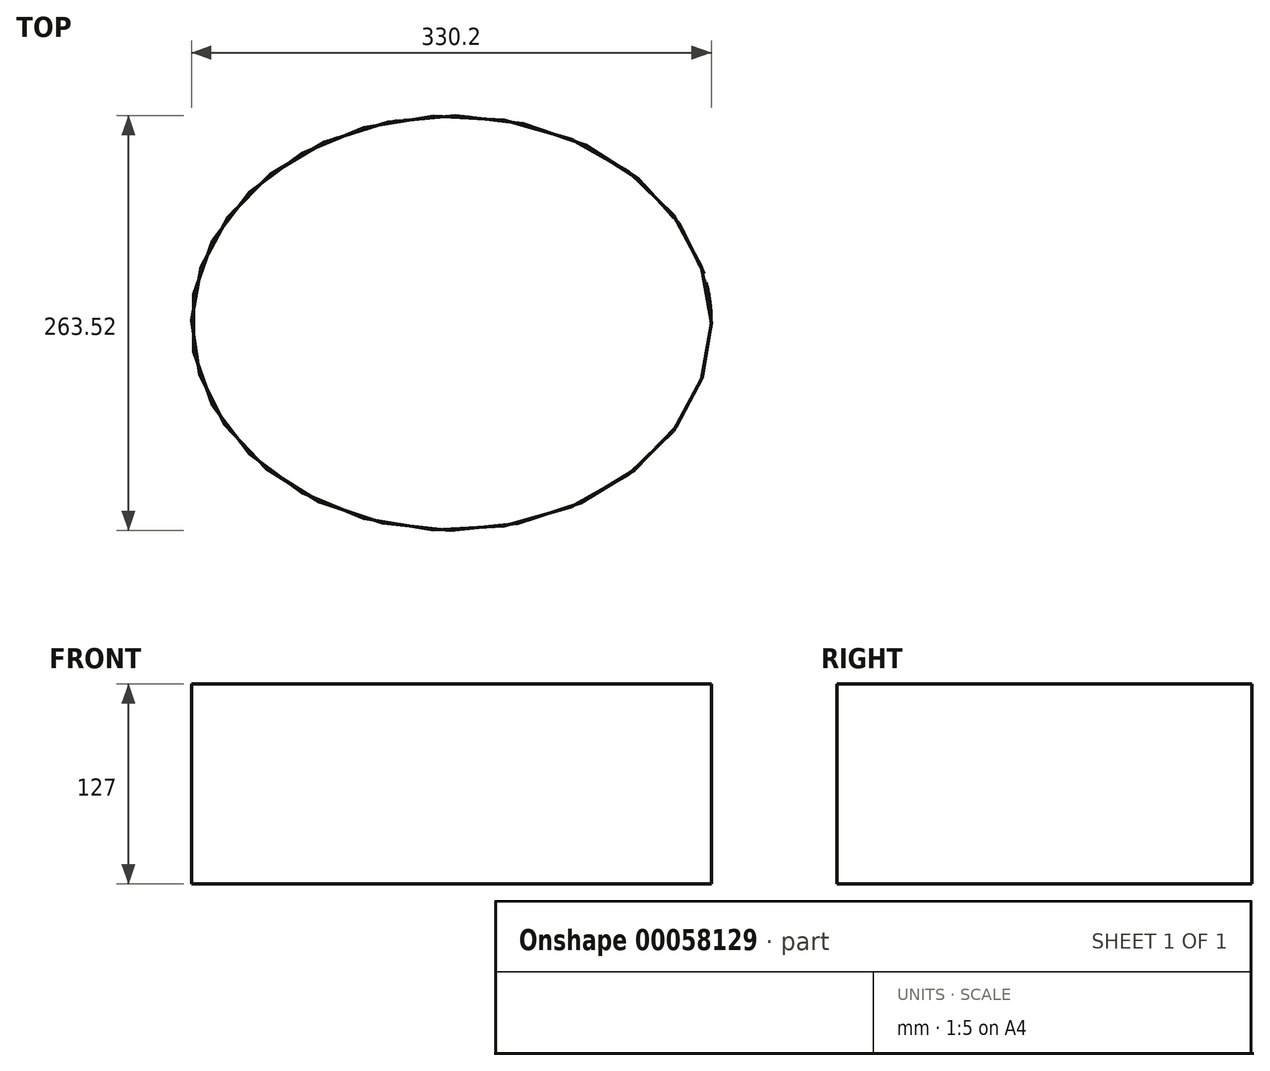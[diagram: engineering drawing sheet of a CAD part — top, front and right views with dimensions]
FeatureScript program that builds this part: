
annotation { "Feature Type Name" : "Feature", "Feature Type Description" : "" }
export const myFeature = defineFeature(function(context is Context, id is Id, definition is map)
    precondition{}
    {
        {
            var Q0;
            Q0=qCreatedBy(makeId("Top.planeOp"),FACE);
            var sketch = newSketch(context, id + "F0", { "sketchPlane" : qUnion([Q0])});
            skEllipse(sketch, "E0", {"center": v(0, 0) * mm, "majorRadius": 165.1 * mm, "minorRadius": 131.76 * mm, "majorAxis": v(1, 0)});
            skFitSpline(sketch, "E1.0", {"points": [v(158.72, -3.08) * mm, v(158.77, 0) * mm, v(158.72, 3.08) * mm, v(158.53, 7.16) * mm, v(158.05, 12.25) * mm, v(157.11, 18.3) * mm, v(155.36, 26.3) * mm, v(152.27, 36.12) * mm, v(147.13, 47.57) * mm, v(140.6, 58.6) * mm, v(134.02, 67.37) * mm, v(128.1, 74.1) * mm, v(123.33, 78.99) * mm, v(119.1, 82.92) * mm, v(115.54, 85.97) * mm, v(112.8, 88.22) * mm, v(109.98, 90.4) * mm, v(106.14, 93.25) * mm, v(101.2, 96.65) * mm, v(95.03, 100.48) * mm, v(86.52, 105.26) * mm, v(75.37, 110.58) * mm, v(61.29, 115.89) * mm, v(46.6, 120.09) * mm, v(33.95, 122.63) * mm, v(23.64, 124.06) * mm, v(15.83, 124.84) * mm, v(9.26, 125.23) * mm, v(3.98, 125.39) * mm, v(0, 125.43) * mm, v(-3.98, 125.39) * mm, v(-9.26, 125.23) * mm, v(-15.83, 124.84) * mm, v(-23.64, 124.06) * mm, v(-33.95, 122.63) * mm, v(-46.6, 120.09) * mm, v(-61.29, 115.89) * mm, v(-75.37, 110.58) * mm, v(-86.52, 105.26) * mm, v(-95.03, 100.48) * mm, v(-101.2, 96.65) * mm, v(-106.14, 93.25) * mm, v(-109.98, 90.4) * mm, v(-112.8, 88.22) * mm, v(-115.54, 85.97) * mm, v(-119.1, 82.92) * mm, v(-123.33, 78.99) * mm, v(-128.1, 74.1) * mm, v(-134.02, 67.37) * mm, v(-140.6, 58.6) * mm, v(-147.13, 47.57) * mm, v(-152.27, 36.12) * mm, v(-155.36, 26.3) * mm, v(-157.11, 18.3) * mm, v(-158.05, 12.25) * mm, v(-158.53, 7.16) * mm, v(-158.72, 3.08) * mm, v(-158.77, 0) * mm, v(-158.72, -3.08) * mm, v(-158.53, -7.16) * mm, v(-158.05, -12.25) * mm, v(-157.11, -18.3) * mm, v(-155.36, -26.3) * mm, v(-152.27, -36.12) * mm, v(-147.13, -47.57) * mm, v(-140.6, -58.6) * mm, v(-134.02, -67.37) * mm, v(-128.1, -74.1) * mm, v(-123.33, -78.99) * mm, v(-119.1, -82.92) * mm, v(-115.54, -85.97) * mm, v(-112.8, -88.22) * mm, v(-109.98, -90.4) * mm, v(-106.14, -93.25) * mm, v(-101.2, -96.65) * mm, v(-95.03, -100.48) * mm, v(-86.52, -105.26) * mm, v(-75.37, -110.58) * mm, v(-61.29, -115.89) * mm, v(-46.6, -120.09) * mm, v(-33.95, -122.63) * mm, v(-23.64, -124.06) * mm, v(-15.83, -124.84) * mm, v(-9.26, -125.23) * mm, v(-3.98, -125.39) * mm, v(0, -125.43) * mm, v(3.98, -125.39) * mm, v(9.26, -125.23) * mm, v(15.83, -124.84) * mm, v(23.64, -124.06) * mm, v(33.95, -122.63) * mm, v(46.6, -120.09) * mm, v(61.29, -115.89) * mm, v(75.37, -110.58) * mm, v(86.52, -105.26) * mm, v(95.03, -100.48) * mm, v(101.2, -96.65) * mm, v(106.14, -93.25) * mm, v(109.98, -90.4) * mm, v(112.8, -88.22) * mm, v(115.54, -85.97) * mm, v(119.1, -82.92) * mm, v(123.33, -78.99) * mm, v(128.1, -74.1) * mm, v(134.02, -67.37) * mm, v(140.6, -58.6) * mm, v(147.13, -47.57) * mm, v(152.27, -36.12) * mm, v(155.36, -26.3) * mm, v(157.11, -18.3) * mm, v(158.05, -12.25) * mm, v(158.53, -7.16) * mm, v(158.72, -3.08) * mm, v(158.77, 0) * mm, v(158.72, 3.08) * mm, v(158.72, -3.08) * mm]});
            skSolve(sketch);
        }
        {
            var Q0;
            Q0=makeQuery(id+"F0.imprint","IMPRINT",FACE,{"disambiguationData":[TD([[makeQuery(id+"F0.imprint","IMPRINT",EDGE,{"derivedFrom":sQuery(id+"F0.wireOp",EDGE,"E0")}),1.0]])]});
            extrude(context, id + "F1", {"entities" : qUnion([Q0]), "depth" : 25.4 * mm});
        }
        {
            var Q0;
            Q0=qCreatedBy(makeId("Top.planeOp"),FACE);
            var sketch = newSketch(context, id + "F2", { "sketchPlane" : qUnion([Q0])});
            skEllipse(sketch, "E2", {"center": v(0, 0) * mm, "majorRadius": 165.1 * mm, "minorRadius": 131.76 * mm, "majorAxis": v(1, 0)});
            skFitSpline(sketch, "E3.0", {"points": [v(158.72, -3.08) * mm, v(158.77, 0) * mm, v(158.72, 3.08) * mm, v(158.53, 7.16) * mm, v(158.05, 12.25) * mm, v(157.1, 18.3) * mm, v(155.36, 26.3) * mm, v(152.27, 36.12) * mm, v(147.13, 47.57) * mm, v(140.6, 58.6) * mm, v(134.02, 67.37) * mm, v(128.1, 74.1) * mm, v(123.33, 78.98) * mm, v(119.1, 82.92) * mm, v(115.54, 85.97) * mm, v(112.8, 88.22) * mm, v(109.98, 90.4) * mm, v(106.14, 93.25) * mm, v(101.2, 96.65) * mm, v(95.03, 100.48) * mm, v(86.52, 105.26) * mm, v(75.37, 110.58) * mm, v(61.29, 115.89) * mm, v(46.6, 120.09) * mm, v(33.95, 122.63) * mm, v(23.64, 124.06) * mm, v(15.83, 124.84) * mm, v(9.26, 125.23) * mm, v(3.98, 125.39) * mm, v(0, 125.43) * mm, v(-3.98, 125.39) * mm, v(-9.26, 125.23) * mm, v(-15.83, 124.84) * mm, v(-23.64, 124.06) * mm, v(-33.95, 122.63) * mm, v(-46.6, 120.09) * mm, v(-61.29, 115.89) * mm, v(-75.37, 110.58) * mm, v(-86.52, 105.26) * mm, v(-95.03, 100.48) * mm, v(-101.2, 96.65) * mm, v(-106.14, 93.25) * mm, v(-109.98, 90.4) * mm, v(-112.8, 88.22) * mm, v(-115.54, 85.97) * mm, v(-119.1, 82.92) * mm, v(-123.33, 78.98) * mm, v(-128.1, 74.1) * mm, v(-134.02, 67.37) * mm, v(-140.6, 58.6) * mm, v(-147.13, 47.57) * mm, v(-152.27, 36.12) * mm, v(-155.36, 26.3) * mm, v(-157.11, 18.3) * mm, v(-158.05, 12.25) * mm, v(-158.53, 7.16) * mm, v(-158.72, 3.08) * mm, v(-158.77, 0) * mm, v(-158.72, -3.08) * mm, v(-158.53, -7.16) * mm, v(-158.05, -12.25) * mm, v(-157.11, -18.3) * mm, v(-155.36, -26.3) * mm, v(-152.27, -36.12) * mm, v(-147.13, -47.57) * mm, v(-140.6, -58.6) * mm, v(-134.02, -67.37) * mm, v(-128.1, -74.1) * mm, v(-123.33, -78.99) * mm, v(-119.1, -82.92) * mm, v(-115.54, -85.97) * mm, v(-112.8, -88.22) * mm, v(-109.98, -90.4) * mm, v(-106.14, -93.25) * mm, v(-101.2, -96.65) * mm, v(-95.03, -100.48) * mm, v(-86.52, -105.26) * mm, v(-75.37, -110.58) * mm, v(-61.29, -115.89) * mm, v(-46.6, -120.09) * mm, v(-33.95, -122.63) * mm, v(-23.64, -124.06) * mm, v(-15.83, -124.84) * mm, v(-9.26, -125.23) * mm, v(-3.98, -125.39) * mm, v(0, -125.43) * mm, v(3.98, -125.39) * mm, v(9.26, -125.23) * mm, v(15.83, -124.84) * mm, v(23.64, -124.06) * mm, v(33.95, -122.63) * mm, v(46.6, -120.09) * mm, v(61.29, -115.89) * mm, v(75.37, -110.58) * mm, v(86.52, -105.26) * mm, v(95.03, -100.48) * mm, v(101.2, -96.65) * mm, v(106.14, -93.25) * mm, v(109.98, -90.4) * mm, v(112.8, -88.22) * mm, v(115.54, -85.97) * mm, v(119.1, -82.92) * mm, v(123.33, -78.99) * mm, v(128.1, -74.1) * mm, v(134.02, -67.37) * mm, v(140.6, -58.6) * mm, v(147.13, -47.57) * mm, v(152.27, -36.12) * mm, v(155.36, -26.3) * mm, v(157.1, -18.3) * mm, v(158.05, -12.25) * mm, v(158.53, -7.16) * mm, v(158.72, -3.08) * mm, v(158.77, 0) * mm, v(158.72, 3.08) * mm, v(158.72, -3.08) * mm]});
            skSolve(sketch);
        }
        {
            var Q0;
            Q0=makeQuery(id+"F2.imprint","IMPRINT",FACE,{"disambiguationData":[TD([[makeQuery(id+"F2.imprint","IMPRINT",EDGE,{"derivedFrom":sQuery(id+"F2.wireOp",EDGE,"E2")}),1.0]])]});
            extrude(context, id + "F3", {"entities" : qUnion([Q0]), "operationType" : NewBodyOperationType.ADD, "oppositeDirection" : true, "depth" : 101.6 * mm});
        }
    });
